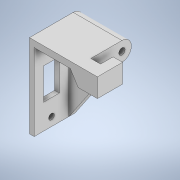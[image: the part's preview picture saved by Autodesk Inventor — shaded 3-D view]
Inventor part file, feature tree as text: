
AUTODESK INVENTOR PART (.ipt)
format: ipt  version: 2022 (Build 260153000, 153)  size: 216,576 bytes
history: native  units: in
note: dims shown in document units (in); Inventor stores cm internally (conversion verified against a paired STEP export)
features: extrude x10, sketch x10, chamfer x1
ambient origin geometry x8: Origin, YZ Plane, XZ Plane, XY Plane, X Axis, Y Axis, Z Axis, Center Point
bodies: Solid1 (feature_tree)
feature tree (21):
  extrude  "Extrusion1"  Depth=0.122in
  extrude  "Extrusion2"  Depth=0.1181in
  extrude  "Extrusion3"  Depth=0.2362in TaperAngle=0.0deg
  extrude  "Extrusion4"  Depth=0.0787in
  extrude  "Extrusion5"  Depth=0.315in
  extrude  "Extrusion6"  Depth=0.5118in
  extrude  "Extrusion7"  Depth=0.5512in
  extrude  "Extrusion8"  Depth=0.1575in
  extrude  "Extrusion9"  Depth=0.1575in
  extrude  "Extrusion10"  Depth=0.3937in TaperAngle=0.0deg
  chamfer  "Chamfer1"  Distance=0.3937in
  sketch  "Sketch1"  dims[d1=0.6693in d2=0.122in]
  sketch  "Sketch2"  dims[d3=0.1181in d4=0.1181in]
  sketch  "Sketch3"  dims[d5=0.2441in d6=0.2362in d7=0.0in]
  sketch  "Sketch4"  dims[d8=0.122in d9=0.0787in]
  sketch  "Sketch5"  dims[d10=0.2362in d11=0.0in d13=0.315in]
  sketch  "Sketch7"  dims[d14=0.3937in d15=0.0in d17=0.5118in]
  sketch  "Sketch8"  dims[d18=0.4921in d19=0.5512in]
  sketch  "Sketch9"  dims[d20=0.1575in d21=0.0in d22=0.0984in]
  sketch  "Sketch11"  dims[d23=0.1575in d24=0.0in d25=0.4528in]
  sketch  "Sketch13"  dims[d26=0.4331in d27=0.3937in d28=0.0in d29=0.3937in d30=0.0in d31=0.4331in d32=1.0433in d33=0.0in d34=0.0787in d35=0.0in d36=0.1083in d37=0.1083in d38=0.0709in d39=0.0709in d40=0.3937in d41=0.1969in d42=0.1181in d43=0.2165in d44=0.2165in d45=0.0787in d46=0.0in d47=0.0984in d48=0.1575in d49=45.0deg]
